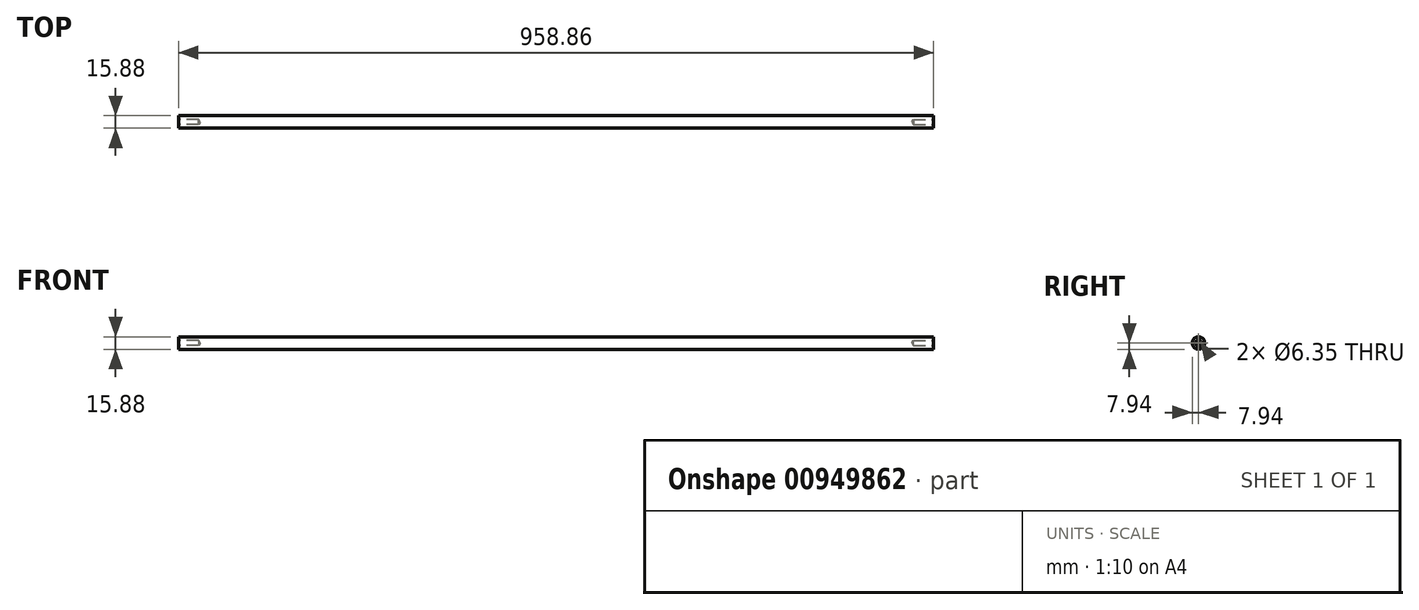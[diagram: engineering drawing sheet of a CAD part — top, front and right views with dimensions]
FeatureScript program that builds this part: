
annotation { "Feature Type Name" : "Feature", "Feature Type Description" : "" }
export const myFeature = defineFeature(function(context is Context, id is Id, definition is map)
    precondition{}
    {
        {
            var Q0;
            Q0=qCreatedBy(makeId("Right.planeOp"),FACE);
            var sketch = newSketch(context, id + "F0", { "sketchPlane" : qUnion([Q0])});
            skCircle(sketch, "E0", {"center": v(0, 0) * mm, "radius": 7.94 * mm});
            skSolve(sketch);
        }
        {
            var Q0;
            Q0=qSketchRegion(id+"F0",true);
            extrude(context, id + "F1", {"entities" : qUnion([Q0]), "endBound" : BoundingType.SYMMETRIC, "depth" : 958.85 * mm, "offsetDistance" : 25.4 * mm});
        }
        {
            var Q0;
            Q0=makeQuery(id+"F1.opExtrude","CAP_FACE",FACE,{"disambiguationData":[OSD([sQuery(id+"F0.wireOp",EDGE,"E0")])],"isStart":true});
            var sketch = newSketch(context, id + "F2", { "sketchPlane" : qUnion([Q0])});
            skLineSegment(sketch, "E1", {"start": v(-7.94, 0) * mm, "end": v(7.94, 0) * mm, "construction": true});
            skPoint(sketch, "E2", {"position": v(0, 0) * mm});
            skSolve(sketch);
        }
        {
            var Q0;
            Q0=sQuery(id+"F2.wireOp",VERTEX,"E2");
            var Q1;
            Q1=makeQuery(id+"F1.opExtrude","SWEPT_BODY",BODY,{"disambiguationData":[OSD([sQuery(id+"F0.wireOp",EDGE,"cLFccdGf-OxBj-Mmzj-VUNQ-G3eTCJfl1HSF.bottom"),sQuery(id+"F0.wireOp",EDGE,"cLFccdGf-OxBj-Mmzj-VUNQ-G3eTCJfl1HSF.top"),sQuery(id+"F0.wireOp",EDGE,"cLFccdGf-OxBj-Mmzj-VUNQ-G3eTCJfl1HSF.left"),sQuery(id+"F0.wireOp",EDGE,"cLFccdGf-OxBj-Mmzj-VUNQ-G3eTCJfl1HSF.right")])]});
            var Q2;
            Q2=makeQuery(id+"F1.opExtrude","SWEPT_BODY",BODY,{"disambiguationData":[OSD([sQuery(id+"F0.wireOp",EDGE,"E0")])]});
            hole(context, id + "F3", {"style" : HoleStyle.C_SINK, "endStyle" : HoleEndStyle.BLIND, "holeDiameter" : 6.35 * mm, "cSinkDiameter" : 7.62 * mm, "cSinkAngle" : 90 * degree, "majorDiameter" : 6.35 * mm, "holeDepth" : 25.4 * mm, "isTappedThrough" : true, "tappedDepth" : 12.7 * mm, "tapClearance" : 3, "startFromSketch" : true, "locations" : qUnion([Q0]), "scope" : qUnion([Q1, Q2])});
        }
        {
            var Q0;
            Q0=makeQuery(id+"F1.opExtrude","CAP_FACE",FACE,{"disambiguationData":[OSD([sQuery(id+"F0.wireOp",EDGE,"E0")])],"isStart":false});
            var sketch = newSketch(context, id + "F4", { "sketchPlane" : qUnion([Q0])});
            skLineSegment(sketch, "E3", {"start": v(-7.94, 0) * mm, "end": v(7.94, 0) * mm, "construction": true});
            skPoint(sketch, "E4", {"position": v(0, 0) * mm});
            skSolve(sketch);
        }
        {
            var Q0;
            Q0=sQuery(id+"F4.wireOp",VERTEX,"E4");
            var Q1;
            Q1=makeQuery(id+"F1.opExtrude","SWEPT_BODY",BODY,{"disambiguationData":[OSD([sQuery(id+"F0.wireOp",EDGE,"E0")])]});
            hole(context, id + "F5", {"style" : HoleStyle.C_SINK, "endStyle" : HoleEndStyle.BLIND, "holeDiameter" : 6.35 * mm, "cSinkDiameter" : 7.62 * mm, "cSinkAngle" : 90 * degree, "majorDiameter" : 6.35 * mm, "holeDepth" : 25.4 * mm, "isTappedThrough" : true, "tappedDepth" : 12.7 * mm, "tapClearance" : 3, "startFromSketch" : true, "locations" : qUnion([Q0]), "scope" : qUnion([Q1])});
        }
    });
